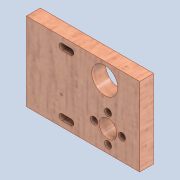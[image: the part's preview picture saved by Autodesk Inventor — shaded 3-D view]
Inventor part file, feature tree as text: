
AUTODESK INVENTOR PART (.ipt)
format: ipt  version: 2020 (Build 240168000, 168)  size: 244,736 bytes
history: native  units: mm
features: extrude x4, sketch x4, other x2, projected_geometry x1, reference x1
ambient origin geometry x8: Origin, YZ Plane, XZ Plane, XY Plane, X Axis, Y Axis, Z Axis, Center Point
bodies: Solid1 (feature_tree)
feature tree (12):
  extrude  "Extrusion1"  Depth=45.0mm
  extrude  "Extrusion3"  Depth=8.0mm
  extrude  "Extrusion4"  Depth=3.5mm
  extrude  "Extrusion5"  TaperAngle=0.0deg  [1 undecoded]
  sketch  "Sketch1"  dims[d0=65.0mm d1=45.0mm]
  sketch  "Sketch3"  dims[d2=8.0mm d3=0.0mm d8=5.0mm]
  projected_geometry  "Projected Loop1"
  sketch  "Sketch4"  dims[d9=3.5mm d10=5.0mm]
  sketch  "Sketch5"  dims[d12=0.0mm d13=0.0mm d14=0.0mm d15=0.0mm d16=5.0mm d17=23.0mm d18=5.0mm d19=8.0mm d20=10.2mm d21=4.1mm d22=4.1mm d23=4.1mm d24=4.1mm d25=22.0mm d26=18.139532mm d27=8.0mm d28=8.0mm d29=8.0mm d30=12.5mm d31=15.0mm d32=23.0mm d33=20.0mm d34=10.0mm d35=0.0mm d36=23.0mm]
  reference  "Reference4"
  other  "0005-10-04 Z axis and extruder.iam"
  other  "0005-10-004 Actionare 2 seringa.ipt:42"
note: 1 required parameter value undecoded (feature->parameter linkage not recoverable at this tier; creation-order binding heuristic only, values carry confidence <= 0.55)
